# Revit family: Diverter_Valve-Three_Way-American_Standard-R433_Series
name_source: partatom
category: Pipe Accessories
units: mm (PartAtom-declared; Revit-internal decimal feet)

## family parameters
Cut with Voids When Loaded = No
Host = Face
OmniClass Number = 23.65.55.14.17
OmniClass Title = Adjusting/Controlling Valves for Liquid Services
Part Type = Normal
Round Connector Dimension = Use Diameter
Shared = Yes

## types (2) — shared parameters
Assembly Code = D2090900
Connection Distance from Finished Wall (1-3/4" to 2-3/4") = 1 3/4"
Default Elevation = 34"
Description = 3-Way In-Wall Diverter Valve Body (Discrete Functions)
Finish = Metal-American Standard-Forged Brass
Height = 3 1/8"
Installation Type = In wall
Length = 1 3/4"
Manufacturer = American Standard
Material = Metal-American Standard-Forged Brass
Price = Prices may vary. Please consult Manufacturer Representative for most up-to-date price list.
Product Documentation Link = https://www.americanstandard-us.com
Product Page URL = https://www.americanstandard-us.com
Tempered Water Connection Diameter = 1/2"
URL = https://www.americanstandard-us.com
Width = 3 1/8"

## per-type parameters (varying)
| type | 3 Dicrete/3 Shared Functions | 3 Discrete Functions |
| R433 | No | Yes |
| R433S | Yes | No |

note: column(s) folded — value = type name in every type: Model

## geometry (parser evidence)
native form markers: Sweep x3
no freeform markers — native parametric forms only
